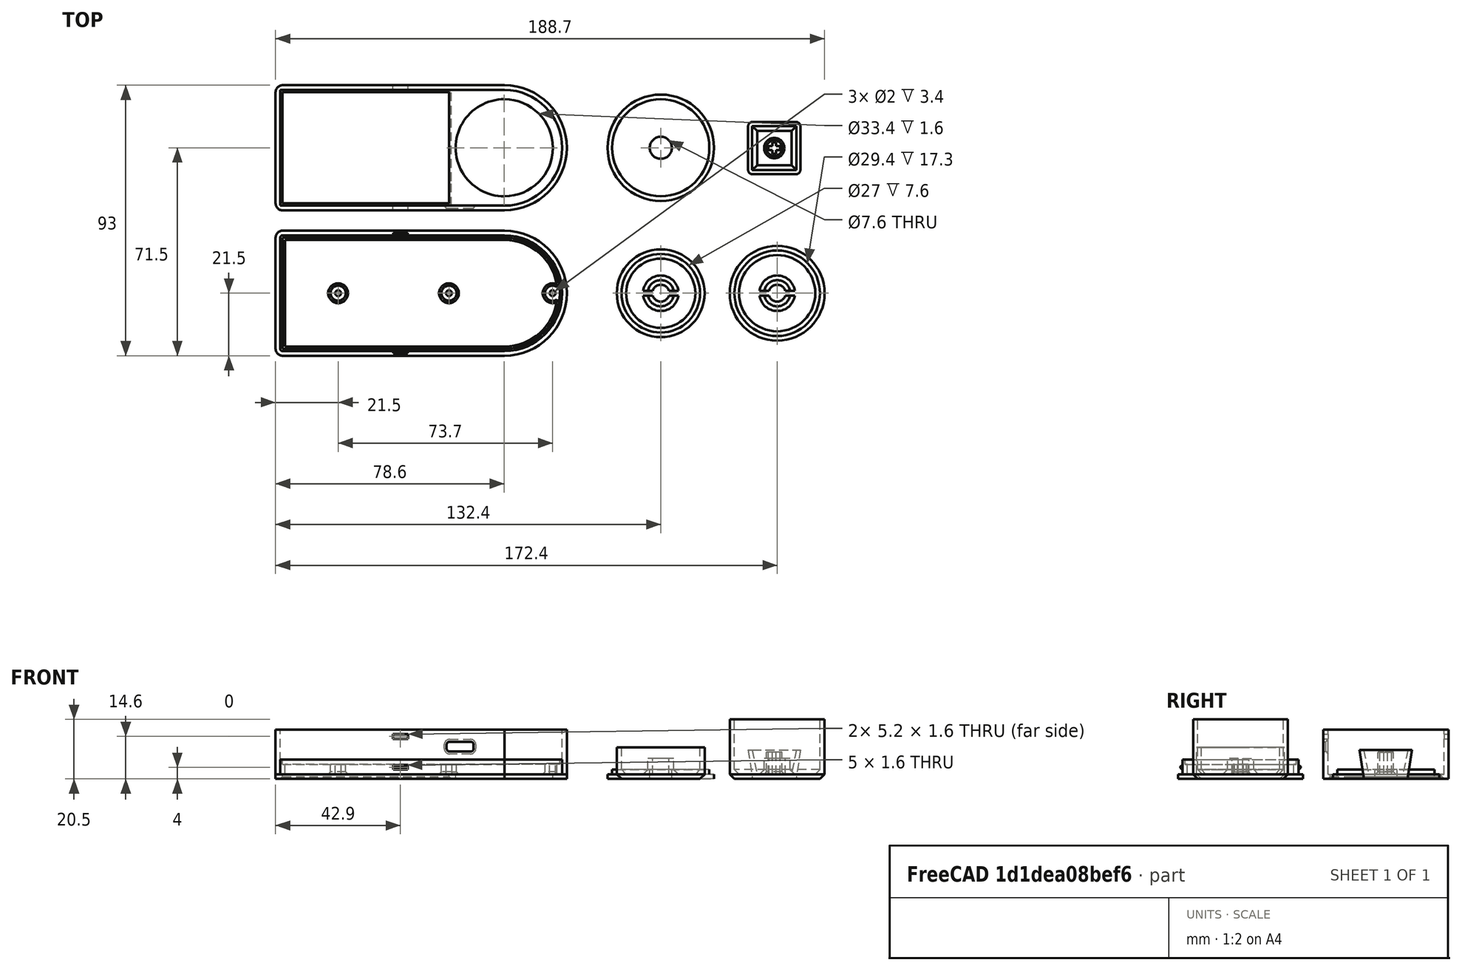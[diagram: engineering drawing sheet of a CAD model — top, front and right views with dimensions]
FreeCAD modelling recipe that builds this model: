
FCSTD DOCUMENT  (FreeCAD 0.19R)
Label: MacroPadPlus_USBC
License: All rights reserved
LicenseURL: http://en.wikipedia.org/wiki/All_rights_reserved
objects: Part::Cylinder×25, Part::Cut×18, Part::Box×15, Part::MultiFuse×15, Part::Chamfer×14, Part::Fillet×5, Part::Wedge×2
note: 94 computed .brp shape members not serialized (recipe doc carries the construction recipe); baked Part::Feature solids carry a one-line shape summary decoded from their .brp

FEATURE [Part::Box] Box  label="Würfel"
  AttacherType = Attacher::AttachEngine3D
  Height = 1.6
  Length = 78.7
  Placement = pos=(-2.4,-2.4,0) rot=(0,0,1;0rad)
  Width = 43
FEATURE [Part::Box] Box001  label="Würfel001"
  AttacherType = Attacher::AttachEngine3D
  Height = 6.6
  Length = 77.1
  Placement = pos=(-0.8,-0.8,0) rot=(0,0,1;0rad)
  Width = 39.8
FEATURE [Part::Box] Box002  label="Würfel002"
  AttacherType = Attacher::AttachEngine3D
  Height = 1.6
  Length = 76.3
  Placement = pos=(0,0,5) rot=(0,0,1;0rad)
  Width = 38.2
FEATURE [Part::Cylinder] Cylinder  label="Zylinder"
  Angle = 360
  AttacherType = Attacher::AttachEngine3D
  Height = 1.6
  Placement = pos=(76.2,19.1,0) rot=(0,0,1;0rad)
  Radius = 21.5
FEATURE [Part::Cylinder] Cylinder001  label="Zylinder001"
  Angle = 360
  AttacherType = Attacher::AttachEngine3D
  Height = 6.6
  Placement = pos=(76.2,19.1,0) rot=(0,0,1;0rad)
  Radius = 19.9
FEATURE [Part::Cylinder] Cylinder002  label="Zylinder002"
  Angle = 360
  AttacherType = Attacher::AttachEngine3D
  Height = 1.6
  Placement = pos=(76.2,19.1,5) rot=(0,0,1;0rad)
  Radius = 19.1
FEATURE [Part::Box] Box003  label="Würfel003"
  AttacherType = Attacher::AttachEngine3D
  Height = 5
  Length = 75.5
  Placement = pos=(0.8,0.8,1.6) rot=(0,0,1;0rad)
  Width = 36.6
FEATURE [Part::Cylinder] Cylinder003  label="Zylinder003"
  Angle = 360
  AttacherType = Attacher::AttachEngine3D
  Height = 5
  Placement = pos=(76.2,19.1,1.6) rot=(0,0,1;0rad)
  Radius = 18.3
FEATURE [Part::MultiFuse] Fusion
  Shapes = -> [Box,Cylinder]
FEATURE [Part::MultiFuse] Fusion001
  Shapes = -> [Box001,Cylinder001]
FEATURE [Part::MultiFuse] Fusion002
  Shapes = -> [Box002,Cylinder002]
FEATURE [Part::MultiFuse] Fusion003
  Shapes = -> [Box003,Cylinder003]
FEATURE [Part::MultiFuse] Fusion004
  Shapes = -> [Fusion,Fusion001]
FEATURE [Part::MultiFuse] Fusion005
  Shapes = -> [Fusion002,Fusion003]
FEATURE [Part::Cut] Cut
  Base = -> Fusion004
  Tool = -> Fusion005
FEATURE [Part::Fillet] Fillet
  Base = -> Cut
  Edges = 2 edges r=0.8: [Edge30,Edge31]
FEATURE [Part::Fillet] Fillet001
  Base = -> Fillet
  Edges = 2 edges r=2.4: [Edge24,Edge27]
FEATURE [Part::Cylinder] Cylinder004  label="Zylinder004"
  Angle = 360
  AttacherType = Attacher::AttachEngine3D
  Height = 5
  Placement = pos=(19.1,19.1,0) rot=(0,0,1;0rad)
  Radius = 2.6
FEATURE [Part::Cylinder] Cylinder005  label="Zylinder005"
  Angle = 360
  AttacherType = Attacher::AttachEngine3D
  Height = 5
  Placement = pos=(19.1,19.1,1.6) rot=(0,0,1;0rad)
  Radius = 1
FEATURE [Part::Cut] Cut001
  Base = -> Cylinder004
  Tool = -> Cylinder005
FEATURE [Part::Cylinder] Cylinder006  label="Zylinder006"
  Angle = 360
  AttacherType = Attacher::AttachEngine3D
  Height = 5
  Placement = pos=(57.2,19.1,0) rot=(0,0,1;0rad)
  Radius = 2.6
FEATURE [Part::Cylinder] Cylinder007  label="Zylinder007"
  Angle = 360
  AttacherType = Attacher::AttachEngine3D
  Height = 5
  Placement = pos=(57.2,19.1,1.6) rot=(0,0,1;0rad)
  Radius = 1
FEATURE [Part::Cut] Cut002
  Base = -> Cylinder006
  Tool = -> Cylinder007
FEATURE [Part::Cylinder] Cylinder008  label="Zylinder008"
  Angle = 360
  AttacherType = Attacher::AttachEngine3D
  Height = 5
  Placement = pos=(92.8,19.1,0) rot=(0,0,1;0rad)
  Radius = 2.6
FEATURE [Part::Cylinder] Cylinder009  label="Zylinder009"
  Angle = 360
  AttacherType = Attacher::AttachEngine3D
  Height = 5
  Placement = pos=(92.8,19.1,1.6) rot=(0,0,1;0rad)
  Radius = 1
FEATURE [Part::Cut] Cut003
  Base = -> Cylinder008
  Tool = -> Cylinder009
FEATURE [Part::MultiFuse] Fusion006
  Shapes = -> [Fillet001,Cut002,Cut001,Cut003]
FEATURE [Part::Chamfer] Chamfer
  Base = -> Fusion006
  Edges = 1 edges r=0.8: [Edge178]
FEATURE [Part::Chamfer] Chamfer001
  Base = -> Chamfer
  Edges = 1 edges r=0.8: [Edge4]
FEATURE [Part::Chamfer] Chamfer002
  Base = -> Chamfer001
  Edges = 1 edges r=0.8: [Edge33]
FEATURE [Part::Box] Box004  label="Würfel004"
  AttacherType = Attacher::AttachEngine3D
  Height = 1.6
  Length = 5
  Placement = pos=(38,39,3.2) rot=(0,0,1;0rad)
  Width = 0.8
FEATURE [Part::Box] Box005  label="Würfel005"
  AttacherType = Attacher::AttachEngine3D
  Height = 1.6
  Length = 5
  Placement = pos=(38,-1.6,3.2) rot=(0,0,1;0rad)
  Width = 0.8
FEATURE [Part::Chamfer] Chamfer003
  Base = -> Box005
  Edges = 2 edges r=0.6: [Edge9,Edge10]
FEATURE [Part::Chamfer] Chamfer004
  Base = -> Box004
  Edges = 2 edges r=0.6: [Edge11,Edge12]
FEATURE [Part::MultiFuse] Fusion007  label="Bottom"
  Shapes = -> [Chamfer002,Chamfer003,Chamfer004]
FEATURE [Part::Box] Box006  label="Würfel006"
  AttacherType = Attacher::AttachEngine3D
  Height = 17
  Length = 78.7
  Placement = pos=(-2.4,47.6,0) rot=(0,0,1;0rad)
  Width = 43
FEATURE [Part::Cylinder] Cylinder010  label="Zylinder010"
  Angle = 360
  AttacherType = Attacher::AttachEngine3D
  Height = 17
  Placement = pos=(76.2,69.1,0) rot=(0,0,1;0rad)
  Radius = 21.5
FEATURE [Part::Box] Box007  label="Würfel007"
  AttacherType = Attacher::AttachEngine3D
  Height = 17
  Length = 77.1
  Placement = pos=(-0.8,49.2,1.6) rot=(0,0,1;0rad)
  Width = 39.8
FEATURE [Part::Cylinder] Cylinder011  label="Zylinder011"
  Angle = 360
  AttacherType = Attacher::AttachEngine3D
  Height = 17
  Placement = pos=(76.2,69.1,1.6) rot=(0,0,1;0rad)
  Radius = 19.9
FEATURE [Part::MultiFuse] Fusion008
  Shapes = -> [Box006,Cylinder010]
FEATURE [Part::MultiFuse] Fusion009
  Shapes = -> [Box007,Cylinder011]
FEATURE [Part::Cut] Cut004
  Base = -> Fusion008
  Tool = -> Fusion009
FEATURE [Part::Fillet] Fillet002
  Base = -> Cut004
  Edges = 2 edges r=2.4: [Edge1,Edge3]
FEATURE [Part::Cylinder] Cylinder012  label="Zylinder012"
  Angle = 360
  AttacherType = Attacher::AttachEngine3D
  Height = 1.6
  Placement = pos=(76.2,69.1,0) rot=(0,0,1;0rad)
  Radius = 16.7
FEATURE [Part::Box] Box008  label="Würfel008"
  AttacherType = Attacher::AttachEngine3D
  Height = 1.6
  Length = 57.2
  Placement = pos=(0,50,0) rot=(0,0,1;0rad)
  Width = 38.2
FEATURE [Part::Cut] Cut005
  Base = -> Fillet002
  Tool = -> Cylinder012
FEATURE [Part::Cut] Cut006
  Base = -> Cut005
  Tool = -> Box008
FEATURE [Part::Chamfer] Chamfer005
  Base = -> Cut006
  Edges = 6 edges r=0.8: [Edge20,Edge21,Edge22,Edge23,Edge24,Edge47]
FEATURE [Part::Cylinder] Cylinder013  label="Zylinder013"
  Angle = 360
  AttacherType = Attacher::AttachEngine3D
  Height = 3.2
  Placement = pos=(130,69.1,0) rot=(0,0,1;0rad)
  Radius = 16.7
FEATURE [Part::Cylinder] Cylinder014  label="Zylinder014"
  Angle = 360
  AttacherType = Attacher::AttachEngine3D
  Height = 1.6
  Placement = pos=(130,69.1,0) rot=(0,0,1;0rad)
  Radius = 18.3
FEATURE [Part::MultiFuse] Fusion010
  Shapes = -> [Cylinder013,Cylinder014]
FEATURE [Part::Cylinder] Cylinder015  label="Zylinder015"
  Angle = 360
  AttacherType = Attacher::AttachEngine3D
  Height = 3.2
  Placement = pos=(130,69.1,0) rot=(0,0,1;0rad)
  Radius = 3.8
FEATURE [Part::Cut] Cut007  label="Ring"
  Base = -> Fusion010
  Tool = -> Cylinder015
FEATURE [Part::Cylinder] Cylinder016  label="Zylinder016"
  Angle = 360
  AttacherType = Attacher::AttachEngine3D
  Height = 10.8
  Placement = pos=(130,19.1,0) rot=(0,0,1;0rad)
  Radius = 15.1
FEATURE [Part::Cylinder] Cylinder017  label="Zylinder017"
  Angle = 360
  AttacherType = Attacher::AttachEngine3D
  Height = 10.8
  Placement = pos=(130,19.1,1.6) rot=(0,0,1;0rad)
  Radius = 13.5
FEATURE [Part::Cut] Cut008
  Base = -> Cylinder016
  Tool = -> Cylinder017
FEATURE [Part::Chamfer] Chamfer006
  Base = -> Cut008
  Edges = 1 edges r=1.6: [Edge6]
FEATURE [Part::Chamfer] Chamfer007
  Base = -> Chamfer006
  Edges = 1 edges r=1.6: [Edge8]
FEATURE [Part::Cylinder] Cylinder018  label="Zylinder018"
  Angle = 360
  AttacherType = Attacher::AttachEngine3D
  Height = 7
  Placement = pos=(130,19.1,0) rot=(0,0,1;0rad)
  Radius = 4.5
FEATURE [Part::Cylinder] Cylinder019  label="Zylinder019"
  Angle = 360
  AttacherType = Attacher::AttachEngine3D
  Height = 10.5
  Placement = pos=(130,19.1,1.6) rot=(0,0,1;0rad)
  Radius = 2.9
FEATURE [Part::Cut] Cut009
  Base = -> Cylinder018
  Tool = -> Cylinder019
FEATURE [Part::MultiFuse] Fusion011
  Shapes = -> [Chamfer007,Cut009]
FEATURE [Part::Chamfer] Chamfer008
  Base = -> Fusion011
  Edges = 1 edges r=1.6: [Edge12]
FEATURE [Part::Box] Box009  label="Würfel009"
  AttacherType = Attacher::AttachEngine3D
  Height = 10.5
  Length = 15
  Placement = pos=(123,18.3,1.6) rot=(0,0,1;0rad)
  Width = 1.6
FEATURE [Part::Cut] Cut010  label="Knob"
  Base = -> Chamfer008
  Tool = -> Box009
FEATURE [Part::Box] Box010  label="Würfel010"
  AttacherType = Attacher::AttachEngine3D
  Height = 1.6
  Length = 5.2
  Placement = pos=(37.9,45,13.8) rot=(0,0,1;0rad)
  Width = 50
FEATURE [Part::Cut] Cut011
  Base = -> Chamfer005
  Tool = -> Box010
FEATURE [Part::Box] Box011  label="Würfel011"
  AttacherType = Attacher::AttachEngine3D
  Height = 3.4
  Length = 9.2
  Placement = pos=(56.4,45,9.4) rot=(0,0,1;0rad)
  Width = 10
FEATURE [Part::Wedge] Wedge  label="Keil"
  AttacherType = Attacher::AttachEngine3D
  Placement = pos=(170,20,10) rot=(-1,0,0;1.5708rad)
  X2max = 16.5
  X2min = 1.5
  Xmax = 18
  Xmin = 0
  Ymax = 10
  Ymin = 0
  Z2max = 16.5
  Z2min = 1.5
  Zmax = 18
  Zmin = 0
FEATURE [Part::Wedge] Wedge001  label="Keil001"
  AttacherType = Attacher::AttachEngine3D
  Placement = pos=(171.4,21.4,10) rot=(-1,0,0;1.5708rad)
  X2max = 13.5
  X2min = 1.7
  Xmax = 15.2
  Xmin = 0
  Ymax = 8.4
  Ymin = 0
  Z2max = 13.5
  Z2min = 1.7
  Zmax = 15.2
  Zmin = 0
FEATURE [Part::Cut] Cut013
  Base = -> Wedge
  Tool = -> Wedge001
FEATURE [Part::Fillet] Fillet004
  Base = -> Cut013
  Edges = 4 edges r=1.6: [Edge2,Edge4,Edge13,Edge16]
FEATURE [Part::Cylinder] Cylinder020  label="Zylinder020"
  Angle = 360
  AttacherType = Attacher::AttachEngine3D
  Height = 9.2
  Placement = pos=(179,29,0) rot=(0,0,1;0rad)
  Radius = 2.7
FEATURE [Part::MultiFuse] Fusion012
  Shapes = -> [Fillet004,Cylinder020]
FEATURE [Part::Chamfer] Chamfer009
  Base = -> Fusion012
  Edges = 1 edges r=0.8: [Edge3]
FEATURE [Part::Box] Box012  label="Würfel012"
  AttacherType = Attacher::AttachEngine3D
  Height = 10
  Length = 4
  Placement = pos=(177,28.35,1.6) rot=(0,0,1;0rad)
  Width = 1.3
FEATURE [Part::Box] Box013  label="Würfel013"
  AttacherType = Attacher::AttachEngine3D
  Height = 10
  Length = 4
  Placement = pos=(179.65,27,1.6) rot=(0,0,1;1.5708rad)
  Width = 1.3
FEATURE [Part::MultiFuse] Fusion013
  Shapes = -> [Box012,Box013]
FEATURE [Part::Cut] Cut014  label="Keycap"
  Base = -> Chamfer009
  Placement = pos=(-10,40,0) rot=(0,0,1;0rad)
  Tool = -> Fusion013
FEATURE [Part::Cylinder] Cylinder021  label="Zylinder021"
  Angle = 360
  AttacherType = Attacher::AttachEngine3D
  Height = 20.5
  Placement = pos=(130,19.1,0) rot=(0,0,1;0rad)
  Radius = 16.3
FEATURE [Part::Cylinder] Cylinder022  label="Zylinder022"
  Angle = 360
  AttacherType = Attacher::AttachEngine3D
  Height = 20.5
  Placement = pos=(130,19.1,1.6) rot=(0,0,1;0rad)
  Radius = 14.7
FEATURE [Part::Cut] Cut015
  Base = -> Cylinder021
  Tool = -> Cylinder022
FEATURE [Part::Chamfer] Chamfer010
  Base = -> Cut015
  Edges = 1 edges r=1.6: [Edge6]
FEATURE [Part::Chamfer] Chamfer011
  Base = -> Chamfer010
  Edges = 1 edges r=1.6: [Edge8]
FEATURE [Part::Cylinder] Cylinder023  label="Zylinder023"
  Angle = 360
  AttacherType = Attacher::AttachEngine3D
  Height = 7
  Placement = pos=(130,19.1,0) rot=(0,0,1;0rad)
  Radius = 4.5
FEATURE [Part::Cylinder] Cylinder024  label="Zylinder024"
  Angle = 360
  AttacherType = Attacher::AttachEngine3D
  Height = 10.5
  Placement = pos=(130,19.1,1.6) rot=(0,0,1;0rad)
  Radius = 2.9
FEATURE [Part::Cut] Cut016
  Base = -> Cylinder023
  Tool = -> Cylinder024
FEATURE [Part::MultiFuse] Fusion014
  Shapes = -> [Chamfer011,Cut016]
FEATURE [Part::Chamfer] Chamfer012
  Base = -> Fusion014
  Edges = 1 edges r=1.6: [Edge12]
FEATURE [Part::Box] Box014  label="Würfel014"
  AttacherType = Attacher::AttachEngine3D
  Height = 10.5
  Length = 15
  Placement = pos=(123,18.3,1.6) rot=(0,0,1;0rad)
  Width = 1.6
FEATURE [Part::Cut] Cut017  label="Knob_big"
  Base = -> Chamfer012
  Placement = pos=(40,0,0) rot=(0,0,1;0rad)
  Tool = -> Box014
FEATURE [Part::Fillet] Fillet005  label="USB"
  Base = -> Box011
  Edges = 4 edges r=1: [Edge2,Edge4,Edge6,Edge8]
FEATURE [Part::Cut] Cut018  label="Top_raw"
  Base = -> Cut011
  Tool = -> Fillet005
FEATURE [Part::Chamfer] Chamfer013  label="Top"
  Base = -> Cut018
  Edges = 8 edges r=0.8: [Edge106,Edge108,Edge111,Edge112,Edge114,Edge116,Edge119,Edge120]
